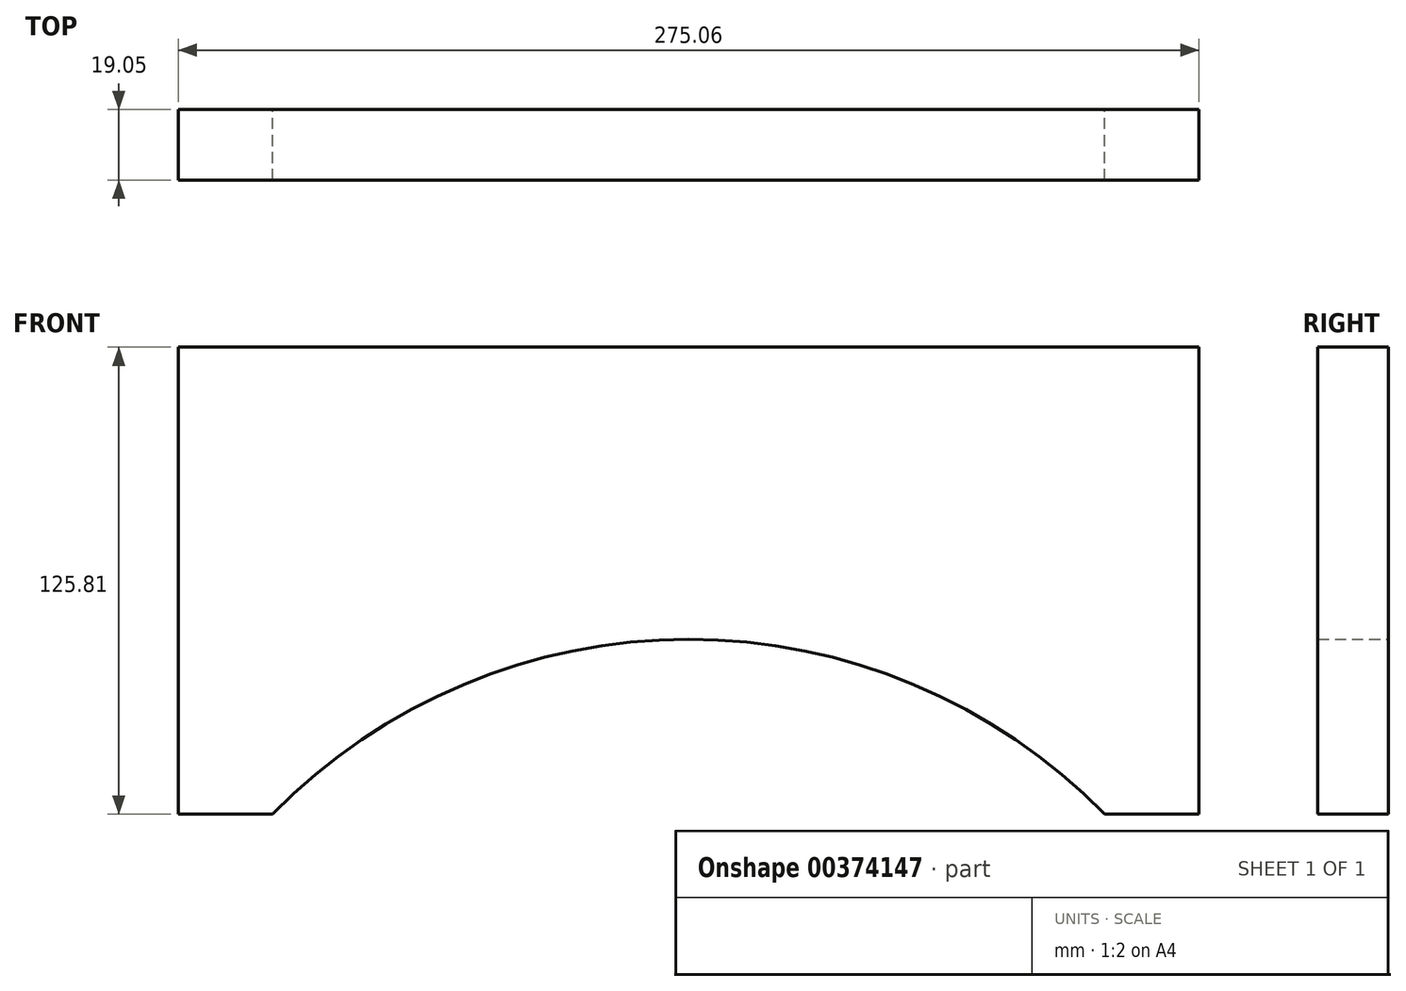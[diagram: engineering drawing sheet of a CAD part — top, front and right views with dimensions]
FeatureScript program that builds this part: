
annotation { "Feature Type Name" : "Feature", "Feature Type Description" : "" }
export const myFeature = defineFeature(function(context is Context, id is Id, definition is map)
    precondition{}
    {
        {
            var Q0;
            Q0=qCreatedBy(makeId("Front.planeOp"),FACE);
            var sketch = newSketch(context, id + "F0", { "sketchPlane" : qUnion([Q0])});
            skLineSegment(sketch, "E0", {"start": v(196.43, 0) * mm, "end": v(-78.63, 0) * mm});
            skLineSegment(sketch, "E1", {"start": v(196.43, 0) * mm, "end": v(196.43, 125.8) * mm});
            skLineSegment(sketch, "E2", {"start": v(0, -72.61) * mm, "end": v(0, 76.65) * mm, "construction": true});
            skLineSegment(sketch, "E3.MirrorCS", {"start": v(69.96, 0) * mm, "end": v(69.96, 21.6) * mm});
            skLineSegment(sketch, "E4", {"start": v(-78.63, 0) * mm, "end": v(-78.63, 125.8) * mm});
            skLineSegment(sketch, "E5", {"start": v(-78.63, 125.8) * mm, "end": v(-53.23, 125.8) * mm});
            skLineSegment(sketch, "E6", {"start": v(171.03, 125.8) * mm, "end": v(196.43, 125.8) * mm});
            skPoint(sketch, "E7.third.point", {"position": v(13.46, -158.17) * mm});
            skPoint(sketch, "E8.first.point", {"position": v(-53.23, 0) * mm});
            skPoint(sketch, "E8.second.point", {"position": v(171.03, 0) * mm});
            skPoint(sketch, "E8.third.point", {"position": v(25.23, -176.3) * mm});
            skLineSegment(sketch, "E9", {"start": v(-53.23, 125.8) * mm, "end": v(171.03, 125.8) * mm});
            skArc(sketch, "E10", {"start": v(171.03, 0) * mm, "mid": v(58.9, 47.1) * mm, "end": v(-53.23, 0) * mm});
            skPoint(sketch, "E10.third.point", {"position": v(9.65, 39.18) * mm});
            skSolve(sketch);
        }
        {
            var Q0;
            Q0=qSketchRegion(id+"F0",true);
            extrude(context, id + "F1", {"entities" : qUnion([Q0]), "depth" : 19.05 * mm});
        }
        {
            var Q0;
            {var subQ2=sQuery(id+"F0.wireOp",EDGE,"E10");Q0=makeQuery(id+"F0.imprint","IMPRINT",FACE,{"disambiguationData":[TD([[makeQuery(id+"F0.imprint","IMPRINT",EDGE,{"derivedFrom":subQ2}),1.0]])]});}
            extrude(context, id + "F2", {"entities" : qUnion([Q0]), "operationType" : NewBodyOperationType.REMOVE, "depth" : 19.05 * mm});
        }
    });
